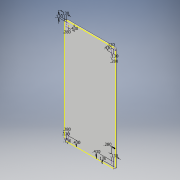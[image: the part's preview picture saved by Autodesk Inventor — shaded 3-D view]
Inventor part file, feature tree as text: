
AUTODESK INVENTOR PART (.ipt)
format: ipt  version: 2019 (Build 230136000, 136)  size: 122,880 bytes
history: native  units: in
note: dims shown in document units (in); Inventor stores cm internally (conversion verified against a paired STEP export)
features: extrude x1, sketch x1, imported_body x1
ambient origin geometry x8: Origin, YZ Plane, XZ Plane, XY Plane, X Axis, Y Axis, Z Axis, Center Point
bodies: Solid1 (feature_tree)
feature tree (3):
  extrude  "Extrusion1"  Depth=7.87in
  sketch  "Sketch2"  dims[d0=3.83in d1=7.87in d2=0.125in d3=0.1in d4=0.0in d5=0.13in d6=0.13in d7=0.13in d8=0.13in d9=0.13in d10=0.13in d11=0.13in d12=0.13in d13=0.43in d14=0.28in d15=0.28in d16=0.43in d17=0.43in d18=0.28in d19=0.43in d20=0.28in d21=1.0in d22=1.0in d23=1.0in d24=0.15in d25=0.25in d26=0.375in d27=0.5635in d28=0.75in d29=0.8108in d30=0.0625in d31=0.75in d32=0.375in]
  imported_body  "Base"
